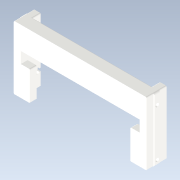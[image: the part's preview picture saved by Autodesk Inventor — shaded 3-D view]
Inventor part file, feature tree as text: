
AUTODESK INVENTOR PART (.ipt)
format: ipt  version: 2022.1 (Build 261234020, 234B)  size: 657,408 bytes
history: native  units: mm
features: projected_geometry x11, delete_face x6, sketch x5, extrude x4, fillet x3, direct_edit x1, hole x1, chamfer x1, other x1, move_body x1
ambient origin geometry x8: Origin, YZ Plane, XZ Plane, XY Plane, X Axis, Y Axis, Z Axis, Center Point
bodies: Volumenkörper1 (feature_tree)
feature tree (34):
  extrude  "Extrusion1"  Depth=6.15mm
  direct_edit  "Direktbearbeitung1"
  delete_face  "Fläche löschen1"
  delete_face  "Fläche löschen2"
  hole  "Bohrung1"  [1 undecoded]
  delete_face  "Fläche löschen3"
  delete_face  "Fläche löschen4"
  extrude  "Extrusion2"  Depth=4.5mm
  delete_face  "Fläche löschen5"
  fillet  "Rundung1"  Radius=4.5mm
  extrude  "Extrusion3"  Depth=4.5mm
  delete_face  "Fläche löschen6"
  fillet  "Rundung2"  [1 undecoded]
  chamfer  "Fase1"  Distance=19.0mm
  extrude  "Extrusion4"  Depth=1.0mm
  fillet  "Rundung3"  Radius=1.799999mm
  sketch  "Skizze1"  dims[d0=6.15mm d1=6.15mm]
  projected_geometry  "Projizierte Kontur1"
  projected_geometry  "Projizierte Kontur2"
  sketch  "Skizze2"  dims[d2=6.15mm d3=6.15mm]
  projected_geometry  "Projizierte Kontur3"
  projected_geometry  "Projizierte Kontur4"
  sketch  "Skizze3"  dims[d4=9.0mm d5=4.5mm d6=4.5mm]
  projected_geometry  "Projizierte Kontur5"
  projected_geometry  "Projizierte Kontur6"
  sketch  "Skizze4"  dims[d7=4.5mm d8=4.5mm d9=0.0mm]
  projected_geometry  "Projizierte Kontur7"
  projected_geometry  "Projizierte Kontur8"
  sketch  "Skizze5"  dims[d10=0.0mm d11=19.0mm d12=1.799999mm d13=1.799999mm d14=1.425mm d15=3.2mm d16=0.0mm d17=0.0mm d18=-2.0mm d19=0.0mm d20=6.9mm d21=3.45mm d22=3.45mm d23=45.0mm d24=10.0mm d25=6.12mm d26=6.0mm d27=4.0mm d28=2.0mm d29=90.0deg d30=3.2mm d31=0.0mm d32=10.0mm d33=0.0mm d34=1.0mm d35=10.0mm d36=0.0mm d37=1.0mm d38=0.4mm d39=2.0mm d40=45.0deg d41=10.0mm d42=0.0mm d43=1.0mm]
  projected_geometry  "Projizierte Kontur9"
  projected_geometry  "Projizierte Kontur10"
  projected_geometry  "Projizierte Kontur11"
  other  "wagomount"
  move_body  "Verschieben1"
note: 2 required parameter values undecoded (feature->parameter linkage not recoverable at this tier; creation-order binding heuristic only, values carry confidence <= 0.55)
